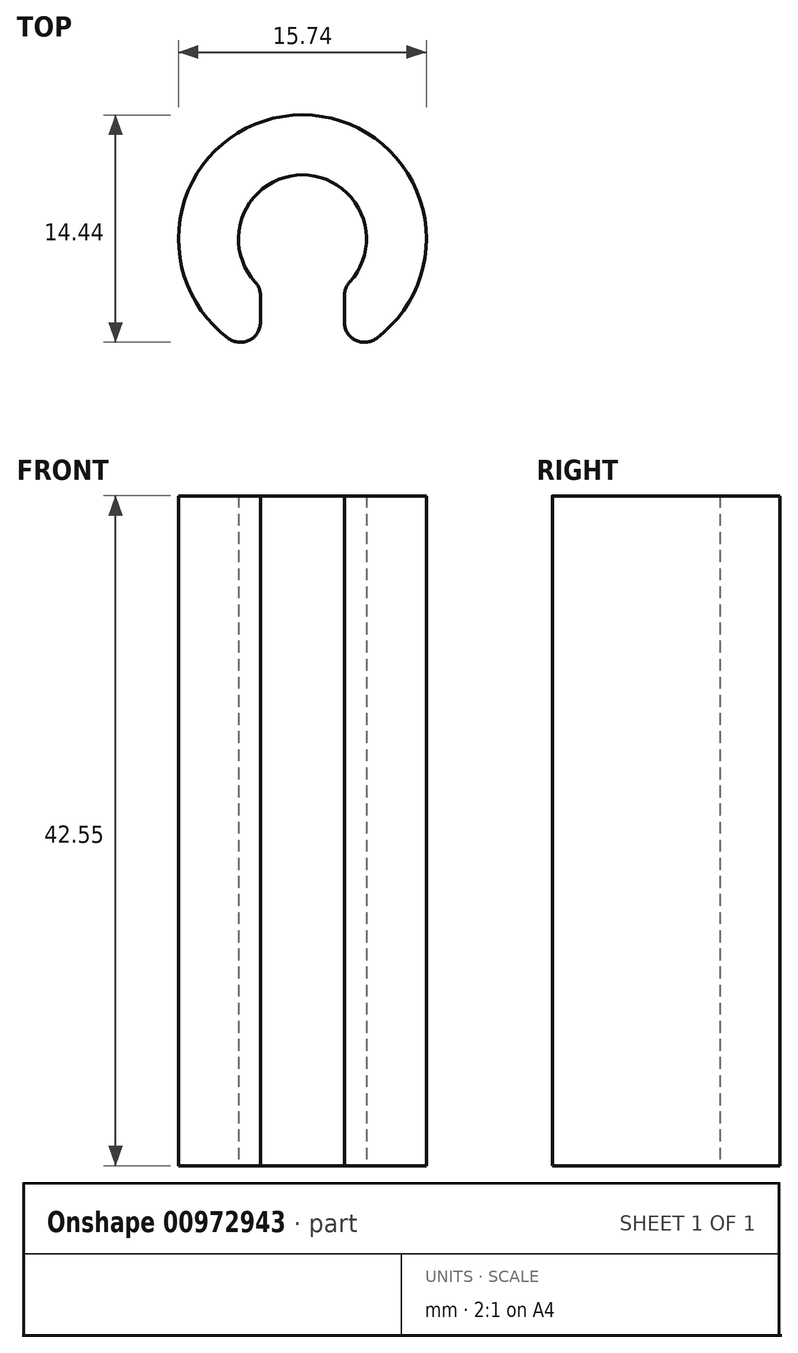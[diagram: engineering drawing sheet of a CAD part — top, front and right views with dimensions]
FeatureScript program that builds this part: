
annotation { "Feature Type Name" : "Feature", "Feature Type Description" : "" }
export const myFeature = defineFeature(function(context is Context, id is Id, definition is map)
    precondition{}
    {
        {
            var Q0;
            Q0=qCreatedBy(makeId("Top.planeOp"),FACE);
            var sketch = newSketch(context, id + "F0", { "sketchPlane" : qUnion([Q0])});
            skArc(sketch, "E0", {"start": v(2.67, -3.07) * mm, "mid": v(0, 4.06) * mm, "end": v(-2.67, -3.07) * mm});
            skArc(sketch, "E1.0", {"start": v(2.67, -7.4) * mm, "mid": v(0, 7.87) * mm, "end": v(-2.67, -7.4) * mm});
            skLineSegment(sketch, "E2", {"start": v(-2.67, -7.4) * mm, "end": v(-2.67, -3.07) * mm});
            skLineSegment(sketch, "E3", {"start": v(2.67, -3.07) * mm, "end": v(2.67, -7.4) * mm});
            skSolve(sketch);
        }
        {
            var Q0;
            Q0=makeQuery(id+"F0.imprint","IMPRINT",FACE,{"disambiguationData":[TD([[makeQuery(id+"F0.imprint","IMPRINT",EDGE,{"derivedFrom":sQuery(id+"F0.wireOp",EDGE,"E0")}),-1.0]])]});
            extrude(context, id + "F1", {"entities" : qUnion([Q0]), "depth" : 42.55 * mm});
        }
        {
            var Q0;
            Q0=makeQuery(id+"F1.opExtrude","SWEPT_EDGE",EDGE,{"disambiguationData":[OSD([sQuery(id+"F0.wireOp",EDGE,"E1.0"),sQuery(id+"F0.wireOp",EDGE,"E2")])]});
            var Q1;
            Q1=makeQuery(id+"F1.opExtrude","SWEPT_EDGE",EDGE,{"disambiguationData":[OSD([sQuery(id+"F0.wireOp",EDGE,"E0"),sQuery(id+"F0.wireOp",EDGE,"E2")])]});
            var Q2;
            Q2=makeQuery(id+"F1.opExtrude","SWEPT_EDGE",EDGE,{"disambiguationData":[OSD([sQuery(id+"F0.wireOp",EDGE,"E1.0"),sQuery(id+"F0.wireOp",EDGE,"E3")])]});
            var Q3;
            Q3=makeQuery(id+"F1.opExtrude","SWEPT_EDGE",EDGE,{"disambiguationData":[OSD([sQuery(id+"F0.wireOp",EDGE,"E0"),sQuery(id+"F0.wireOp",EDGE,"E3")])]});
            fillet(context, id + "F2", {"entities" : qUnion([Q0, Q1, Q2, Q3]), "radius" : 1.27 * mm, "tangentPropagation" : true, "allowEdgeOverflow" : false});
        }
    });
